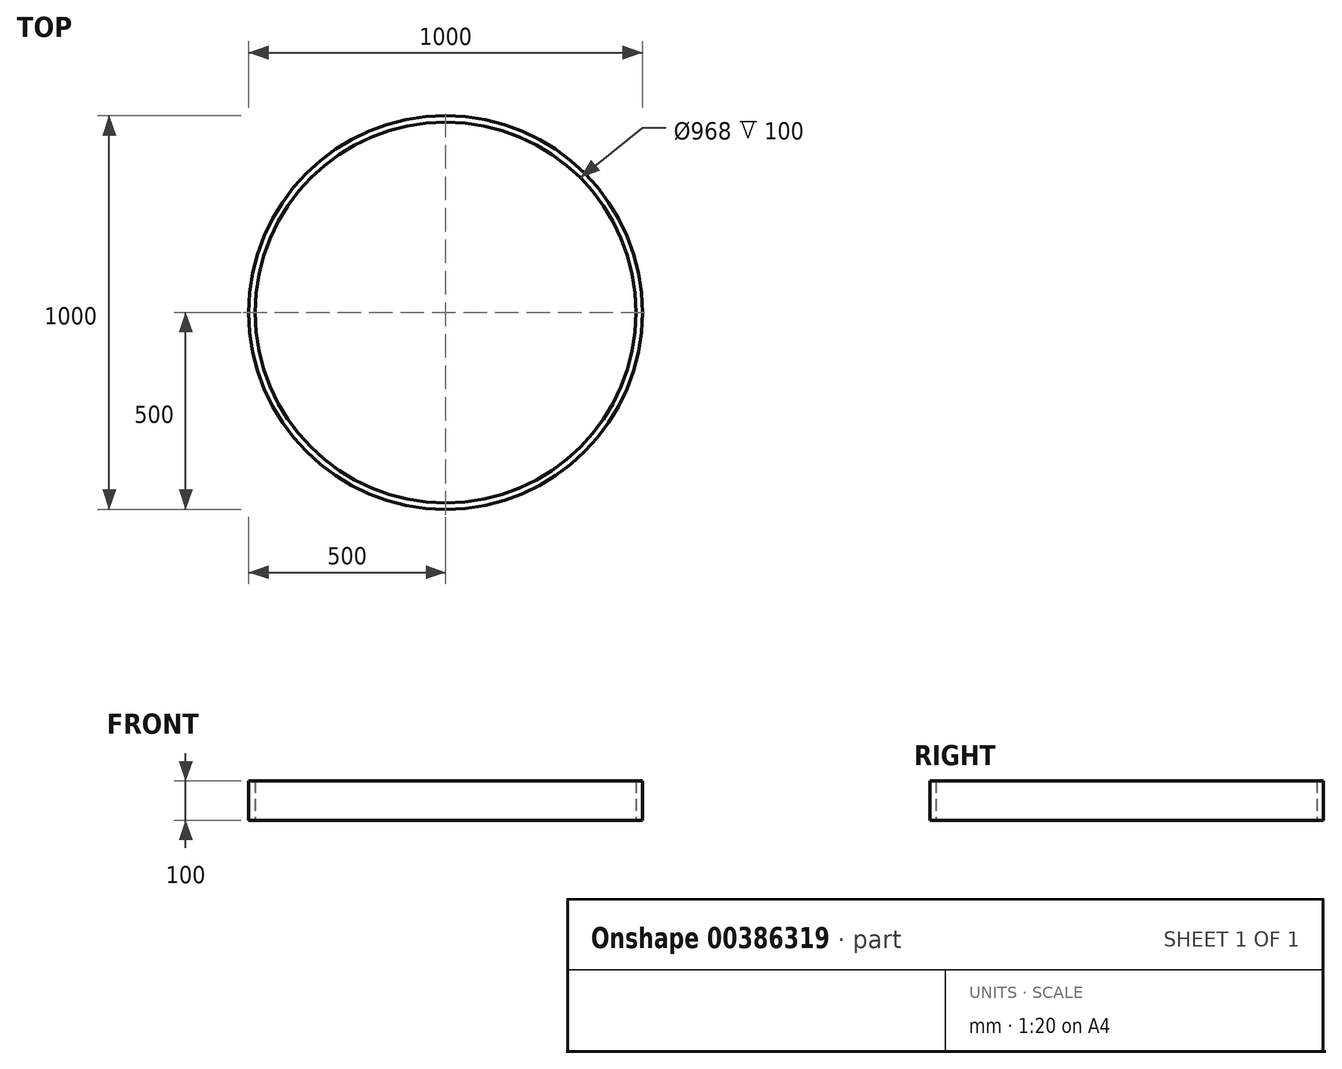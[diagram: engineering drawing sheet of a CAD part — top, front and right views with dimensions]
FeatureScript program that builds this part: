
annotation { "Feature Type Name" : "Feature", "Feature Type Description" : "" }
export const myFeature = defineFeature(function(context is Context, id is Id, definition is map)
    precondition{}
    {
        {
            var Q0;
            Q0=qCreatedBy(makeId("Top.planeOp"),FACE);
            var sketch = newSketch(context, id + "F0", { "sketchPlane" : qUnion([Q0])});
            skCircle(sketch, "E0", {"center": v(0, 0) * mm, "radius": 500 * mm});
            skCircle(sketch, "E1", {"center": v(0, 0) * mm, "radius": 484 * mm});
            skCircle(sketch, "E2.cCircle", {"center": v(0, 0) * mm, "radius": 484 * mm, "construction": true});
            skLineSegment(sketch, "E2.0", {"start": v(0, 484) * mm, "end": v(484, 0) * mm});
            skLineSegment(sketch, "E2.1", {"start": v(484, 0) * mm, "end": v(0, -484) * mm});
            skLineSegment(sketch, "E2.2", {"start": v(0, -484) * mm, "end": v(-484, 0) * mm});
            skLineSegment(sketch, "E2.3", {"start": v(-484, 0) * mm, "end": v(0, 484) * mm});
            skLineSegment(sketch, "E3", {"start": v(0, 484) * mm, "end": v(0, -484) * mm});
            skLineSegment(sketch, "E4", {"start": v(-484, 0) * mm, "end": v(484, 0) * mm});
            skLineSegment(sketch, "E5", {"start": v(-484, 0) * mm, "end": v(-500, 0) * mm});
            skLineSegment(sketch, "E6", {"start": v(0, 484) * mm, "end": v(0, 500) * mm});
            skLineSegment(sketch, "E7", {"start": v(0, -484) * mm, "end": v(0, -500) * mm});
            skLineSegment(sketch, "E8", {"start": v(484, 0) * mm, "end": v(500, 0) * mm});
            skLineSegment(sketch, "E9.2", {"start": v(484, 0) * mm, "end": v(0, 484) * mm});
            skLineSegment(sketch, "E10.bottom", {"start": v(-484, 0) * mm, "end": v(0, 0) * mm});
            skLineSegment(sketch, "E10.right", {"start": v(0, 0) * mm, "end": v(0, 484) * mm});
            skLineSegment(sketch, "E11.right", {"start": v(0, 0) * mm, "end": v(0, -484) * mm});
            skLineSegment(sketch, "E12.bottom", {"start": v(0, 0) * mm, "end": v(500, 0) * mm});
            skLineSegment(sketch, "E12.top", {"start": v(0, 0) * mm, "end": v(500, 0) * mm});
            skLineSegment(sketch, "E12.left", {"start": v(0, 0) * mm, "end": v(0, 0) * mm});
            skLineSegment(sketch, "E12.right", {"start": v(500, 0) * mm, "end": v(500, 0) * mm});
            skLineSegment(sketch, "E13.top", {"start": v(0, 0) * mm, "end": v(484, 0) * mm});
            skLineSegment(sketch, "E13.left", {"start": v(0, -484) * mm, "end": v(0, 0) * mm});
            skSolve(sketch);
        }
        {
            var Q0;
            {var subQ0=sQuery(id+"F0.wireOp",EDGE,"E5");Q0=makeQuery(id+"F0.imprint","IMPRINT",FACE,{"disambiguationData":[TD([[makeQuery(id+"F0.imprint","IMPRINT",EDGE,{"derivedFrom":subQ0}),-1.0]])]});}
            var Q1;
            {var subQ0=sQuery(id+"F0.wireOp",EDGE,"E5");Q1=makeQuery(id+"F0.imprint","IMPRINT",FACE,{"disambiguationData":[TD([[makeQuery(id+"F0.imprint","IMPRINT",EDGE,{"derivedFrom":subQ0}),1.0]])]});}
            var Q2;
            {var subQ0=sQuery(id+"F0.wireOp",EDGE,"E7");Q2=makeQuery(id+"F0.imprint","IMPRINT",FACE,{"disambiguationData":[TD([[makeQuery(id+"F0.imprint","IMPRINT",EDGE,{"derivedFrom":subQ0}),1.0]])]});}
            var Q3;
            {var subQ0=sQuery(id+"F0.wireOp",EDGE,"E6");Q3=makeQuery(id+"F0.imprint","IMPRINT",FACE,{"disambiguationData":[TD([[makeQuery(id+"F0.imprint","IMPRINT",EDGE,{"derivedFrom":subQ0}),-1.0]])]});}
            extrude(context, id + "F1", {"entities" : qUnion([Q0, Q1, Q2, Q3]), "depth" : 100 * mm});
        }
    });
